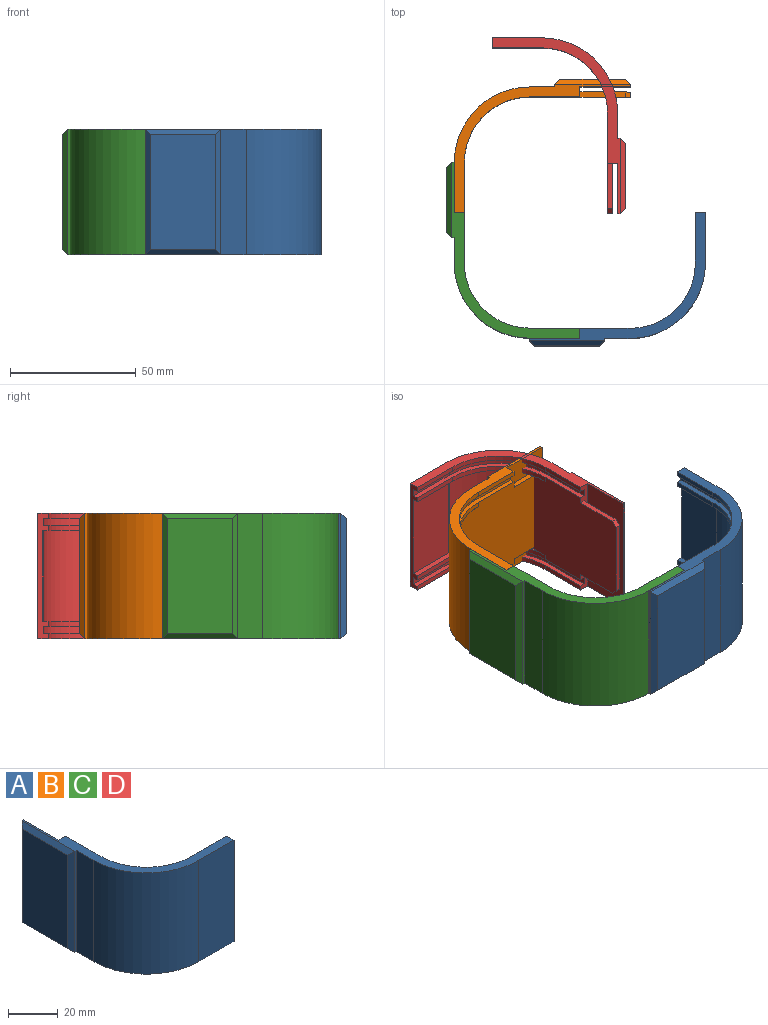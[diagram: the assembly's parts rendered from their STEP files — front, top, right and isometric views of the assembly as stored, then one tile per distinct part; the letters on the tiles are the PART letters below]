
ASSEMBLY  parts=4 mates=3
PART A: 47 faces, bbox 53x70x50 mm
  f0: plane 35x20mm, normal (-1,0,0), area 696mm2, adj f1,f14,f43,f44,f45,f46
  f1: plane 31x2mm, normal (0,1,0), area 62mm2, adj f0,f20,f45,f46
  f2: plane 70x51mm, normal (0,0,1), area 365.9mm2, adj f7,f12,f13,f14,f15,f16,f17,f32
  f3: plane 70x51mm, normal (0,0,-1), area 365.9mm2, adj f7,f12,f13,f14,f29,f30,f31,f32
  f4: plane 46x28.3mm, normal (0,0,-1), area 116.9mm2, adj f5,f13,f20,f21,f22,f41,f42
  f5: cylinder r=28mm len=36mm, axis (0,0,1), area 1200.1mm2, adj f4,f6,f20,f41
  f6: plane 46x28.3mm, normal (0,0,1), area 116.9mm2, adj f5,f13,f20,f23,f24,f41,f42
  f7: plane 50x10mm, normal (-1,0,0), area 500mm2, adj f2,f3,f12,f32
  f8: plane 48x48mm, normal (0,0,-1), area 164.8mm2, adj f13,f14,f20,f23,f24,f25,f26,f27
  f9: plane 20x3mm, normal (0,1,0), area 60mm2, adj f11,f13,f18,f19
  f10: plane 20x3mm, normal (1,0,0), area 60mm2, adj f11,f14,f18,f19
  f11: cylinder r=28mm len=28mm, axis (0,0,-1), area 131.9mm2, adj f9,f10,f18,f19
  f12: cylinder r=30mm len=50mm, axis (0,0,-1), area 2356.2mm2, adj f2,f3,f7,f40
  f13: plane 50x4mm, normal (1,0,0), area 105.2mm2, adj f2,f3,f4,f6,f8,f9,f15,f18
  f14: plane 50x4mm, normal (0,1,0), area 118mm2, adj f0,f2,f3,f8,f10,f17,f18,f19
  f15: plane 20x2mm, normal (0,1,0), area 40mm2, adj f2,f13,f16,f18
  f16: cylinder r=26mm len=26mm, axis (0,0,1), area 81.7mm2, adj f2,f15,f17,f18
  f17: plane 20x2mm, normal (1,0,0), area 40mm2, adj f2,f14,f16,f18
  f18: plane 48x48mm, normal (0,0,-1), area 164.8mm2, adj f9,f10,f11,f13,f14,f15,f16,f17
  f19: plane 48x48mm, normal (0,0,1), area 164.8mm2, adj f9,f10,f11,f13,f14,f20,f21,f22
  f20: plane 50.39x40mm, normal (1,0,0), area 1870.1mm2, adj f1,f4,f5,f6,f8,f14,f19,f21
  f21: cylinder r=26mm len=26mm, axis (0,0,1), area 81.7mm2, adj f4,f19,f20,f22
  f22: plane 20x2mm, normal (0,1,0), area 40mm2, adj f4,f13,f19,f21
  f23: plane 20x2mm, normal (0,1,0), area 40mm2, adj f6,f8,f13,f24
  f24: cylinder r=26mm len=26mm, axis (0,0,1), area 81.7mm2, adj f6,f8,f20,f23
  f25: plane 20x3mm, normal (0,1,0), area 60mm2, adj f8,f13,f27,f28
  f26: plane 20x3mm, normal (1,0,0), area 60mm2, adj f8,f14,f27,f28
  f27: cylinder r=28mm len=28mm, axis (0,0,1), area 131.9mm2, adj f8,f25,f26,f28
  f28: plane 48x48mm, normal (0,0,1), area 164.8mm2, adj f13,f14,f25,f26,f27,f29,f30,f31
  f29: plane 20x2mm, normal (0,1,0), area 40mm2, adj f3,f13,f28,f31
  f30: plane 20x2mm, normal (1,0,0), area 40mm2, adj f3,f14,f28,f31
  f31: cylinder r=26mm len=26mm, axis (0,0,1), area 81.7mm2, adj f3,f28,f29,f30
  f32: plane 50x1mm, normal (0,-1,0), area 50mm2, adj f2,f3,f7,f36
  f33: plane 50x1mm, normal (0,1,0), area 50mm2, adj f2,f3,f35,f39
  f34: plane 46x26mm, normal (-1,0,0), area 1196mm2, adj f36,f37,f38,f39
  f35: plane 50x20mm, normal (1,0,0), area 1000mm2, adj f2,f3,f14,f33
  f36: plane 50x2mm, normal (-0.71,-0.71,0), area 135.8mm2, adj f32,f34,f37,f38
  f37: plane 30x2mm, normal (-0.71,0,0.71), area 79.2mm2, adj f2,f34,f36,f39
  f38: plane 30x2mm, normal (-0.71,0,-0.71), area 79.2mm2, adj f3,f34,f36,f39
  f39: plane 50x2mm, normal (-0.71,0.71,0), area 135.8mm2, adj f33,f34,f37,f38
  f40: plane 50x20mm, normal (0,-1,0), area 1000mm2, adj f2,f3,f12,f13
  f41: plane 36x0.3mm, normal (1,0,0), area 10.8mm2, adj f4,f5,f6,f42
  f42: plane 36x20mm, normal (0,1,0), area 720mm2, adj f4,f6,f13,f41
  f43: plane 18x2mm, normal (0,0,1), area 36mm2, adj f0,f14,f20,f45
  f44: plane 18x2mm, normal (0,0,-1), area 36mm2, adj f0,f14,f20,f46
  f45: plane 2x2mm, normal (0,0.71,0.71), area 5.7mm2, adj f0,f1,f20,f43
  f46: plane 2x2mm, normal (0,0.71,-0.71), area 5.7mm2, adj f0,f1,f20,f44
PART B: same geometry as A
PART C: same geometry as A
PART D: same geometry as A
PLACE A rot(axis=(0,0,1),90deg) t=(57.28,158.56,-132.47)mm
PLACE B rot(axis=(0,0,-1),90deg) t=(-42.63,198.65,-132.47)mm
PLACE C t=(-12.72,128.65,-132.47)mm
PLACE D rot(axis=(0,0,1),180deg) t=(-7.65,248.18,-132.47)mm
MATE fastened B.f13 <-> C.f14  axis (0,-1,0) through (-41.41,178.65,-107.47)mm
MATE fastened D.f2 <-> B.f2  axis (0,0,1) through (7.37,228.65,-82.47)mm
MATE fastened A.f14 <-> C.f13  axis (-1,0,0) through (7.28,129.86,-107.47)mm
